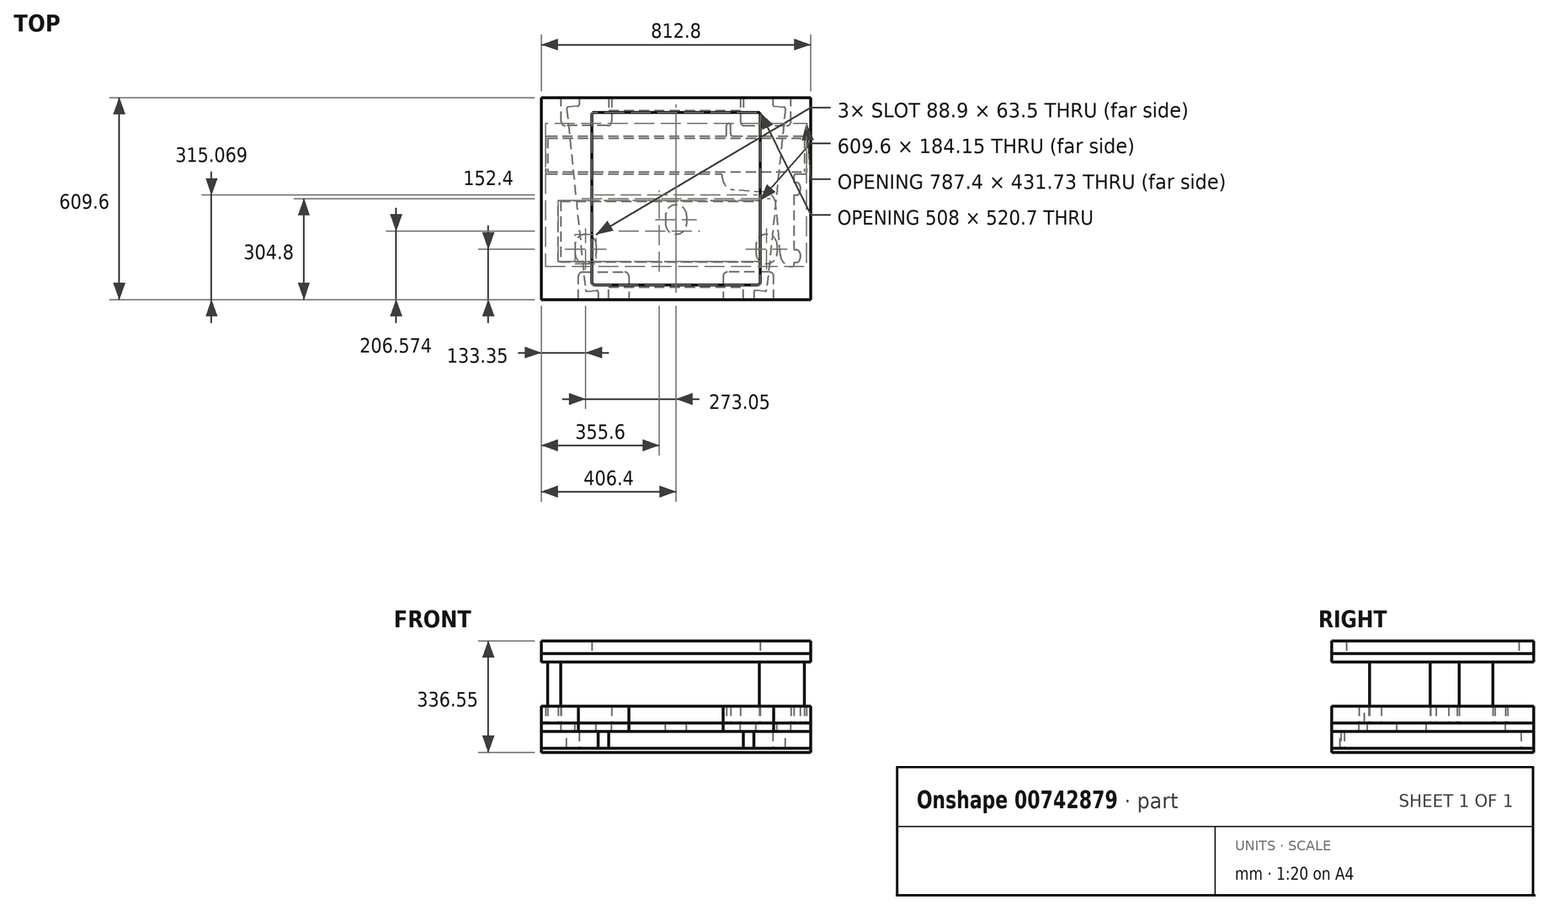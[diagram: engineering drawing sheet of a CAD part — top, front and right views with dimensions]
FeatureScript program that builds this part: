
annotation { "Feature Type Name" : "Feature", "Feature Type Description" : "" }
export const myFeature = defineFeature(function(context is Context, id is Id, definition is map)
    precondition{}
    {
        {
            var Q0;
            Q0=qCreatedBy(makeId("Top.planeOp"),FACE);
            var sketch = newSketch(context, id + "F0", { "sketchPlane" : qUnion([Q0])});
            skLineSegment(sketch, "E0.bottom", {"start": v(-406.4, 304.8) * mm, "end": v(406.4, 304.8) * mm});
            skLineSegment(sketch, "E0.top", {"start": v(-406.4, -304.8) * mm, "end": v(406.4, -304.8) * mm});
            skLineSegment(sketch, "E0.left", {"start": v(-406.4, 304.8) * mm, "end": v(-406.4, -304.8) * mm});
            skLineSegment(sketch, "E0.right", {"start": v(406.4, 304.8) * mm, "end": v(406.4, -304.8) * mm});
            skSolve(sketch);
        }
        {
            var Q0;
            Q0 = qSketchRegion(id + "F0", true);
            extrude(context, id + "F1", {"entities" : qUnion([Q0]), "depth" : 12.7 * mm, "offsetDistance" : 25.4 * mm});
        }
        {
            var Q0;
            Q0=makeQuery(id+"F1.opExtrude","CAP_FACE",FACE,{"disambiguationData":[OSD([sQuery(id+"F0.wireOp",EDGE,"E0.bottom"),sQuery(id+"F0.wireOp",EDGE,"E0.top"),sQuery(id+"F0.wireOp",EDGE,"E0.left"),sQuery(id+"F0.wireOp",EDGE,"E0.right")])],"isStart":false});
            var sketch = newSketch(context, id + "F2", { "sketchPlane" : qUnion([Q0])});
            skLineSegment(sketch, "E1", {"start": v(-292.3, 304.8) * mm, "end": v(-292.3, 279.4) * mm});
            skLineSegment(sketch, "E2", {"start": v(-292.3, 279.4) * mm, "end": v(-330.2, 275.5) * mm});
            skLineSegment(sketch, "E3", {"start": v(-330.2, 275.5) * mm, "end": v(-273.05, -280.37) * mm});
            skLineSegment(sketch, "E4", {"start": v(292.3, 304.8) * mm, "end": v(292.3, 279.4) * mm});
            skLineSegment(sketch, "E5", {"start": v(292.3, 279.4) * mm, "end": v(330.2, 275.5) * mm});
            skLineSegment(sketch, "E6", {"start": v(330.2, 275.5) * mm, "end": v(273.05, -280.37) * mm});
            skLineSegment(sketch, "E7", {"start": v(273.05, -280.37) * mm, "end": v(235.15, -276.47) * mm});
            skLineSegment(sketch, "E8", {"start": v(235.15, -276.47) * mm, "end": v(235.15, -304.8) * mm});
            skLineSegment(sketch, "E9", {"start": v(-273.05, -280.37) * mm, "end": v(-235.15, -276.47) * mm});
            skLineSegment(sketch, "E10", {"start": v(-235.15, -276.47) * mm, "end": v(-235.15, -304.8) * mm});
            skLineSegment(sketch, "E11.bottom", {"start": v(-203.2, 304.8) * mm, "end": v(203.2, 304.8) * mm});
            skLineSegment(sketch, "E11.top", {"start": v(-203.2, 266.7) * mm, "end": v(203.2, 266.7) * mm});
            skLineSegment(sketch, "E11.left", {"start": v(-203.2, 304.8) * mm, "end": v(-203.2, 266.7) * mm});
            skLineSegment(sketch, "E11.right", {"start": v(203.2, 304.8) * mm, "end": v(203.2, 266.7) * mm});
            skLineSegment(sketch, "E12.bottom", {"start": v(-203.2, -304.8) * mm, "end": v(203.2, -304.8) * mm});
            skLineSegment(sketch, "E12.top", {"start": v(-203.2, -266.7) * mm, "end": v(203.2, -266.7) * mm});
            skLineSegment(sketch, "E12.left", {"start": v(-203.2, -304.8) * mm, "end": v(-203.2, -266.7) * mm});
            skLineSegment(sketch, "E12.right", {"start": v(203.2, -304.8) * mm, "end": v(203.2, -266.7) * mm});
            skSolve(sketch);
        }
        {
            var Q0;
            Q0 = qSketchRegion(id + "F2", true);
            var Q1;
            {var subQ2=sQuery(id+"F2.wireOp",EDGE,"E1");Q1=makeQuery(id+"F2.imprint","IMPRINT",FACE,{"disambiguationData":[TD([[makeQuery(id+"F2.imprint","IMPRINT",EDGE,{"derivedFrom":subQ2}),-1.0]])]});}
            var Q2;
            {var subQ3=sQuery(id+"F2.wireOp",EDGE,"E4");Q2=makeQuery(id+"F2.imprint","IMPRINT",FACE,{"disambiguationData":[TD([[makeQuery(id+"F2.imprint","IMPRINT",EDGE,{"derivedFrom":subQ3}),1.0]])]});}
            extrude(context, id + "F3", {"entities" : qUnion([Q0, Q1, Q2]), "depth" : 50.8 * mm, "offsetDistance" : 25.4 * mm});
        }
        {
            var Q0;
            Q0=makeQuery(id+"F1.opExtrude","CAP_FACE",FACE,{"disambiguationData":[OSD([sQuery(id+"F0.wireOp",EDGE,"E0.bottom"),sQuery(id+"F0.wireOp",EDGE,"E0.top"),sQuery(id+"F0.wireOp",EDGE,"E0.left"),sQuery(id+"F0.wireOp",EDGE,"E0.right")])],"isStart":false});
            cPlane(context, id + "F4", {"entities" : qUnion([Q0]), "cplaneType" : CPlaneType.OFFSET, "offset" : 50.8 * mm, "width" : 152.4 * mm, "height" : 152.4 * mm});
        }
        {
            var Q0;
            Q0=qCreatedBy(id+"F4.planeOp",FACE);
            var sketch = newSketch(context, id + "F5", { "sketchPlane" : qUnion([Q0])});
            skLineSegment(sketch, "E13.bottom", {"start": v(-406.4, 304.8) * mm, "end": v(406.4, 304.8) * mm});
            skLineSegment(sketch, "E13.top", {"start": v(-406.4, -304.8) * mm, "end": v(406.4, -304.8) * mm});
            skLineSegment(sketch, "E13.left", {"start": v(-406.4, 304.8) * mm, "end": v(-406.4, -304.8) * mm});
            skLineSegment(sketch, "E13.right", {"start": v(406.4, 304.8) * mm, "end": v(406.4, -304.8) * mm});
            skSolve(sketch);
        }
        {
            var Q0;
            Q0 = qSketchRegion(id + "F5", true);
            extrude(context, id + "F6", {"entities" : qUnion([Q0]), "depth" : 25.4 * mm, "offsetDistance" : 25.4 * mm});
        }
        {
            var Q0;
            Q0=makeQuery(id+"F6.opExtrude","CAP_FACE",FACE,{"disambiguationData":[OSD([sQuery(id+"F5.wireOp",EDGE,"E13.bottom"),sQuery(id+"F5.wireOp",EDGE,"E13.top"),sQuery(id+"F5.wireOp",EDGE,"E13.left"),sQuery(id+"F5.wireOp",EDGE,"E13.right")])],"isStart":false});
            var sketch = newSketch(context, id + "F7", { "sketchPlane" : qUnion([Q0])});
            skLineSegment(sketch, "E14.top", {"start": v(-294.76, -304.8) * mm, "end": v(-142.36, -304.8) * mm});
            skLineSegment(sketch, "E14.right", {"start": v(-142.36, -222.05) * mm, "end": v(-142.36, -304.8) * mm});
            skLineSegment(sketch, "E15", {"start": v(0, 347.7) * mm, "end": v(0, -344.71) * mm});
            skLineSegment(sketch, "E16", {"start": v(-294.76, -304.8) * mm, "end": v(-294.76, -222.05) * mm});
            skLineSegment(sketch, "E17", {"start": v(-294.76, -222.05) * mm, "end": v(-142.36, -222.05) * mm});
            skLineSegment(sketch, "E18.right", {"start": v(-194.32, 304.8) * mm, "end": v(-194.32, 219.79) * mm});
            skLineSegment(sketch, "E19.MirrorCS", {"start": v(142.36, -222.05) * mm, "end": v(142.36, -304.8) * mm});
            skLineSegment(sketch, "E20.MirrorCS", {"start": v(294.76, -304.8) * mm, "end": v(142.36, -304.8) * mm});
            skLineSegment(sketch, "E21.MirrorCS", {"start": v(294.76, -304.8) * mm, "end": v(294.76, -222.05) * mm});
            skLineSegment(sketch, "E22.MirrorCS", {"start": v(194.32, 304.8) * mm, "end": v(194.32, 219.79) * mm});
            skLineSegment(sketch, "E23.MirrorCS", {"start": v(294.76, -222.05) * mm, "end": v(142.36, -222.05) * mm});
            skLineSegment(sketch, "E24", {"start": v(194.32, 219.79) * mm, "end": v(346.72, 219.79) * mm});
            skLineSegment(sketch, "E25", {"start": v(346.72, 219.79) * mm, "end": v(346.72, 304.8) * mm});
            skLineSegment(sketch, "E26", {"start": v(346.72, 304.8) * mm, "end": v(194.32, 304.8) * mm});
            skLineSegment(sketch, "E27", {"start": v(-194.32, 219.79) * mm, "end": v(-346.72, 219.79) * mm});
            skLineSegment(sketch, "E28", {"start": v(-346.72, 219.79) * mm, "end": v(-346.72, 304.8) * mm});
            skLineSegment(sketch, "E29", {"start": v(-346.72, 304.8) * mm, "end": v(-194.32, 304.8) * mm});
            skLineSegment(sketch, "E30.bottom", {"start": v(-273.05, -107.95) * mm, "end": v(-273.05, -107.95) * mm});
            skLineSegment(sketch, "E30.top", {"start": v(-273.05, -196.85) * mm, "end": v(-273.05, -196.85) * mm});
            skLineSegment(sketch, "E30.left", {"start": v(-304.8, -139.7) * mm, "end": v(-304.8, -165.1) * mm});
            skLineSegment(sketch, "E30.right", {"start": v(-241.3, -139.7) * mm, "end": v(-241.3, -165.1) * mm});
            skPoint(sketch, "E30.middle", {"position": v(-273.05, -152.4) * mm});
            skLineSegment(sketch, "E31.bottom", {"start": v(273.05, -107.95) * mm, "end": v(273.05, -107.95) * mm});
            skLineSegment(sketch, "E31.top", {"start": v(273.05, -196.85) * mm, "end": v(273.05, -196.85) * mm});
            skLineSegment(sketch, "E31.left", {"start": v(241.3, -139.7) * mm, "end": v(241.3, -165.1) * mm});
            skLineSegment(sketch, "E31.right", {"start": v(304.8, -139.7) * mm, "end": v(304.8, -165.1) * mm});
            skPoint(sketch, "E31.middle", {"position": v(273.05, -152.4) * mm});
            skLineSegment(sketch, "E32.bottom", {"start": v(0, -19.05) * mm, "end": v(0, -19.05) * mm});
            skLineSegment(sketch, "E32.top", {"start": v(0, -107.95) * mm, "end": v(0, -107.95) * mm});
            skLineSegment(sketch, "E32.left", {"start": v(-31.75, -50.8) * mm, "end": v(-31.75, -76.2) * mm});
            skLineSegment(sketch, "E32.right", {"start": v(31.75, -50.8) * mm, "end": v(31.75, -76.2) * mm});
            skPoint(sketch, "E32.middle", {"position": v(0, -63.5) * mm});
            skPoint(sketch, "E33.0.visualSharp", {"position": v(-304.8, -107.95) * mm});
            skArc(sketch, "E33.0.filletArc", {"start": v(-273.05, -107.95) * mm, "mid": v(-295.5, -117.25) * mm, "end": v(-304.8, -139.7) * mm});
            skPoint(sketch, "E34.0.visualSharp", {"position": v(-241.3, -107.95) * mm});
            skArc(sketch, "E34.0.filletArc", {"start": v(-241.3, -139.7) * mm, "mid": v(-250.6, -117.25) * mm, "end": v(-273.05, -107.95) * mm});
            skPoint(sketch, "E35.0.visualSharp", {"position": v(-304.8, -196.85) * mm});
            skArc(sketch, "E35.0.filletArc", {"start": v(-304.8, -165.1) * mm, "mid": v(-295.5, -187.55) * mm, "end": v(-273.05, -196.85) * mm});
            skPoint(sketch, "E36.0.visualSharp", {"position": v(-241.3, -196.85) * mm});
            skArc(sketch, "E36.0.filletArc", {"start": v(-273.05, -196.85) * mm, "mid": v(-250.6, -187.55) * mm, "end": v(-241.3, -165.1) * mm});
            skPoint(sketch, "E37.0.visualSharp", {"position": v(-31.75, -19.05) * mm});
            skArc(sketch, "E37.0.filletArc", {"start": v(0, -19.05) * mm, "mid": v(-22.45, -28.35) * mm, "end": v(-31.75, -50.8) * mm});
            skPoint(sketch, "E37.1.visualSharp", {"position": v(31.75, -19.05) * mm});
            skArc(sketch, "E37.1.filletArc", {"start": v(31.75, -50.8) * mm, "mid": v(22.45, -28.35) * mm, "end": v(0, -19.05) * mm});
            skPoint(sketch, "E38.0.visualSharp", {"position": v(-31.75, -107.95) * mm});
            skArc(sketch, "E38.0.filletArc", {"start": v(-31.75, -76.2) * mm, "mid": v(-22.45, -98.65) * mm, "end": v(0, -107.95) * mm});
            skPoint(sketch, "E39.0.visualSharp", {"position": v(31.75, -107.95) * mm});
            skArc(sketch, "E39.0.filletArc", {"start": v(0, -107.95) * mm, "mid": v(22.45, -98.65) * mm, "end": v(31.75, -76.2) * mm});
            skPoint(sketch, "E39.1.visualSharp", {"position": v(241.3, -107.95) * mm});
            skArc(sketch, "E39.1.filletArc", {"start": v(273.05, -107.95) * mm, "mid": v(250.6, -117.25) * mm, "end": v(241.3, -139.7) * mm});
            skPoint(sketch, "E39.2.visualSharp", {"position": v(304.8, -107.95) * mm});
            skArc(sketch, "E39.2.filletArc", {"start": v(304.8, -139.7) * mm, "mid": v(295.5, -117.25) * mm, "end": v(273.05, -107.95) * mm});
            skPoint(sketch, "E40.0.visualSharp", {"position": v(304.8, -196.85) * mm});
            skArc(sketch, "E40.0.filletArc", {"start": v(273.05, -196.85) * mm, "mid": v(295.5, -187.55) * mm, "end": v(304.8, -165.1) * mm});
            skPoint(sketch, "E40.1.visualSharp", {"position": v(241.3, -196.85) * mm});
            skArc(sketch, "E40.1.filletArc", {"start": v(241.3, -165.1) * mm, "mid": v(250.6, -187.55) * mm, "end": v(273.05, -196.85) * mm});
            skSolve(sketch);
        }
        {
            var Q0;
            Q0 = qSketchRegion(id + "F7", true);
            extrude(context, id + "F8", {"entities" : qUnion([Q0]), "operationType" : NewBodyOperationType.REMOVE, "oppositeDirection" : true, "depth" : 25.4 * mm, "offsetDistance" : 25.4 * mm});
        }
        {
            var Q0;
            Q0=makeQuery(id+"F6.opExtrude","CAP_FACE",FACE,{"disambiguationData":[OSD([sQuery(id+"F5.wireOp",EDGE,"E13.bottom"),sQuery(id+"F5.wireOp",EDGE,"E13.top"),sQuery(id+"F5.wireOp",EDGE,"E13.left"),sQuery(id+"F5.wireOp",EDGE,"E13.right")])],"isStart":false});
            var sketch = newSketch(context, id + "F9", { "sketchPlane" : qUnion([Q0])});
            skLineSegment(sketch, "E41", {"start": v(-406.4, -304.8) * mm, "end": v(-294.76, -304.8) * mm});
            skLineSegment(sketch, "E42", {"start": v(-294.76, -304.8) * mm, "end": v(-294.76, -222.05) * mm});
            skLineSegment(sketch, "E43", {"start": v(-294.76, -222.05) * mm, "end": v(-142.36, -222.05) * mm});
            skLineSegment(sketch, "E44", {"start": v(-142.36, -222.05) * mm, "end": v(-142.36, -304.8) * mm});
            skLineSegment(sketch, "E45", {"start": v(-142.36, -304.8) * mm, "end": v(142.36, -304.8) * mm});
            skLineSegment(sketch, "E46", {"start": v(142.36, -304.8) * mm, "end": v(142.36, -222.05) * mm});
            skLineSegment(sketch, "E47", {"start": v(142.36, -222.05) * mm, "end": v(294.76, -222.05) * mm});
            skLineSegment(sketch, "E48", {"start": v(294.76, -222.05) * mm, "end": v(294.76, -304.8) * mm});
            skLineSegment(sketch, "E49", {"start": v(294.76, -304.8) * mm, "end": v(406.4, -304.8) * mm});
            skLineSegment(sketch, "E50", {"start": v(194.32, 219.79) * mm, "end": v(194.32, 304.8) * mm});
            skLineSegment(sketch, "E51", {"start": v(194.32, 304.8) * mm, "end": v(-194.32, 304.8) * mm});
            skLineSegment(sketch, "E52", {"start": v(-194.32, 304.8) * mm, "end": v(-194.32, 219.79) * mm});
            skLineSegment(sketch, "E53.bottom", {"start": v(-393.7, 188.04) * mm, "end": v(393.7, 188.04) * mm});
            skLineSegment(sketch, "E53.top", {"start": v(-393.7, 73.74) * mm, "end": v(393.7, 73.74) * mm});
            skLineSegment(sketch, "E53.left", {"start": v(-393.7, 188.04) * mm, "end": v(-393.7, 73.74) * mm});
            skLineSegment(sketch, "E53.right", {"start": v(393.7, 188.04) * mm, "end": v(393.7, 73.74) * mm});
            skLineSegment(sketch, "E54", {"start": v(355.6, 73.74) * mm, "end": v(355.6, -205.66) * mm});
            skLineSegment(sketch, "E55", {"start": v(355.6, -205.66) * mm, "end": v(317.5, -205.66) * mm});
            skLineSegment(sketch, "E56", {"start": v(317.5, -205.66) * mm, "end": v(298.45, 16.59) * mm});
            skLineSegment(sketch, "E57", {"start": v(298.45, 16.59) * mm, "end": v(139.7, 29.29) * mm});
            skLineSegment(sketch, "E58", {"start": v(139.7, 29.29) * mm, "end": v(139.7, 73.74) * mm});
            skLineSegment(sketch, "E59.bottom", {"start": v(165.1, 188.04) * mm, "end": v(152.4, 188.04) * mm});
            skLineSegment(sketch, "E59.top", {"start": v(165.1, 226.14) * mm, "end": v(152.4, 226.14) * mm});
            skLineSegment(sketch, "E59.left", {"start": v(165.1, 188.04) * mm, "end": v(165.1, 226.14) * mm});
            skLineSegment(sketch, "E59.right", {"start": v(152.4, 188.04) * mm, "end": v(152.4, 226.14) * mm});
            skPoint(sketch, "E60.visualSharp", {"position": v(139.7, 29.29) * mm});
            skLineSegment(sketch, "E61", {"start": v(406.4, -304.8) * mm, "end": v(406.4, 304.8) * mm});
            skLineSegment(sketch, "E62", {"start": v(406.4, 304.8) * mm, "end": v(346.72, 304.8) * mm});
            skLineSegment(sketch, "E63", {"start": v(346.72, 304.8) * mm, "end": v(346.72, 219.79) * mm});
            skLineSegment(sketch, "E64", {"start": v(346.72, 219.79) * mm, "end": v(194.32, 219.79) * mm});
            skLineSegment(sketch, "E65", {"start": v(-406.4, -304.8) * mm, "end": v(-406.4, 304.8) * mm});
            skLineSegment(sketch, "E66", {"start": v(-406.4, 304.8) * mm, "end": v(-346.72, 304.8) * mm});
            skLineSegment(sketch, "E67", {"start": v(-346.72, 304.8) * mm, "end": v(-346.72, 219.79) * mm});
            skLineSegment(sketch, "E68", {"start": v(-346.72, 219.79) * mm, "end": v(-194.32, 219.79) * mm});
            skLineSegment(sketch, "E69.bottom", {"start": v(-355.6, -190.3) * mm, "end": v(254, -190.3) * mm});
            skLineSegment(sketch, "E69.top", {"start": v(-355.6, -6.15) * mm, "end": v(254, -6.15) * mm});
            skLineSegment(sketch, "E69.left", {"start": v(-355.6, -190.3) * mm, "end": v(-355.6, -6.15) * mm});
            skLineSegment(sketch, "E69.right", {"start": v(254, -190.3) * mm, "end": v(254, -6.15) * mm});
            skLineSegment(sketch, "E70.bottom", {"start": v(355.6, 48.34) * mm, "end": v(374.65, 48.34) * mm});
            skLineSegment(sketch, "E70.top", {"start": v(355.6, 10.24) * mm, "end": v(374.65, 10.24) * mm});
            skLineSegment(sketch, "E70.left", {"start": v(355.6, 48.34) * mm, "end": v(355.6, 10.24) * mm});
            skLineSegment(sketch, "E70.right", {"start": v(374.65, 48.34) * mm, "end": v(374.65, 10.24) * mm});
            skLineSegment(sketch, "E71.bottom", {"start": v(355.6, -154.86) * mm, "end": v(374.65, -154.86) * mm});
            skLineSegment(sketch, "E71.top", {"start": v(355.6, -192.96) * mm, "end": v(374.65, -192.96) * mm});
            skLineSegment(sketch, "E71.left", {"start": v(355.6, -154.86) * mm, "end": v(355.6, -192.96) * mm});
            skLineSegment(sketch, "E71.right", {"start": v(374.65, -154.86) * mm, "end": v(374.65, -192.96) * mm});
            skSolve(sketch);
        }
        {
            var Q0;
            Q0 = qSketchRegion(id + "F9", true);
            extrude(context, id + "F10", {"entities" : qUnion([Q0]), "depth" : 50.8 * mm, "offsetDistance" : 25.4 * mm});
        }
        {
            var Q0;
            Q0=qCreatedBy(id+"F4.planeOp",FACE);
            cPlane(context, id + "F11", {"entities" : qUnion([Q0]), "cplaneType" : CPlaneType.OFFSET, "offset" : 209.55 * mm, "width" : 152.4 * mm, "height" : 152.4 * mm});
        }
        {
            var Q0;
            Q0=qCreatedBy(id+"F11.planeOp",FACE);
            var sketch = newSketch(context, id + "F12", { "sketchPlane" : qUnion([Q0])});
            skLineSegment(sketch, "E72.bottom", {"start": v(-406.4, -304.8) * mm, "end": v(406.4, -304.8) * mm});
            skLineSegment(sketch, "E72.top", {"start": v(-406.4, 304.8) * mm, "end": v(406.4, 304.8) * mm});
            skLineSegment(sketch, "E72.left", {"start": v(-406.4, -304.8) * mm, "end": v(-406.4, 304.8) * mm});
            skLineSegment(sketch, "E72.right", {"start": v(406.4, -304.8) * mm, "end": v(406.4, 304.8) * mm});
            skSolve(sketch);
        }
        {
            var Q0;
            Q0 = qSketchRegion(id + "F12", true);
            extrude(context, id + "F13", {"entities" : qUnion([Q0]), "depth" : 25.4 * mm, "offsetDistance" : 25.4 * mm});
        }
        {
            var Q0;
            Q0=makeQuery(id+"F13.opExtrude","CAP_FACE",FACE,{"disambiguationData":[OSD([sQuery(id+"F12.wireOp",EDGE,"E72.bottom"),sQuery(id+"F12.wireOp",EDGE,"E72.top"),sQuery(id+"F12.wireOp",EDGE,"E72.left"),sQuery(id+"F12.wireOp",EDGE,"E72.right")])],"isStart":false});
            var sketch = newSketch(context, id + "F14", { "sketchPlane" : qUnion([Q0])});
            skLineSegment(sketch, "E73.bottom", {"start": v(-406.4, 304.8) * mm, "end": v(406.4, 304.8) * mm});
            skLineSegment(sketch, "E73.top", {"start": v(-406.4, -304.8) * mm, "end": v(406.4, -304.8) * mm});
            skLineSegment(sketch, "E73.left", {"start": v(-406.4, 304.8) * mm, "end": v(-406.4, -304.8) * mm});
            skLineSegment(sketch, "E73.right", {"start": v(406.4, 304.8) * mm, "end": v(406.4, -304.8) * mm});
            skLineSegment(sketch, "E74.bottom", {"start": v(-254, 260.35) * mm, "end": v(254, 260.35) * mm});
            skLineSegment(sketch, "E74.top", {"start": v(-254, -260.35) * mm, "end": v(254, -260.35) * mm});
            skLineSegment(sketch, "E74.left", {"start": v(-254, 260.35) * mm, "end": v(-254, -260.35) * mm});
            skLineSegment(sketch, "E74.right", {"start": v(254, 260.35) * mm, "end": v(254, -260.35) * mm});
            skSolve(sketch);
        }
        {
            var Q0;
            Q0 = qSketchRegion(id + "F14", true);
            extrude(context, id + "F15", {"entities" : qUnion([Q0]), "depth" : 38.1 * mm, "offsetDistance" : 25.4 * mm});
        }
        {
            var Q0;
            Q0=makeQuery(id+"F10.opExtrude","SWEPT_EDGE",EDGE,{"disambiguationData":[OSD([sQuery(id+"F9.wireOp",EDGE,"E57"),sQuery(id+"F9.wireOp",EDGE,"E58")])]});
            var Q1;
            Q1=makeQuery(id+"F10.opExtrude","SWEPT_EDGE",EDGE,{"disambiguationData":[OSD([sQuery(id+"F9.wireOp",EDGE,"E56"),sQuery(id+"F9.wireOp",EDGE,"E57")])]});
            var Q2;
            Q2=makeQuery(id+"F10.opExtrude","SWEPT_EDGE",EDGE,{"disambiguationData":[OSD([sQuery(id+"F9.wireOp",EDGE,"E55"),sQuery(id+"F9.wireOp",EDGE,"E56")])]});
            fillet(context, id + "F16", {"entities" : qUnion([Q0, Q1, Q2]), "radius" : 38.1 * mm, "tangentPropagation" : true, "allowEdgeOverflow" : false});
        }
        {
            var Q0;
            Q0=makeQuery(id+"F10.opExtrude","SWEPT_EDGE",EDGE,{"disambiguationData":[OSD([sQuery(id+"F9.wireOp",EDGE,"Z3YEzZHo-Bui1-ousJ-slzW-WUeqwLS6bUEM.top"),sQuery(id+"F9.wireOp",EDGE,"gvYDkn1p-4vf0-wHje-2ojT-luJldiSQSmDk.top"),sQuery(id+"F9.wireOp",EDGE,"gvYDkn1p-4vf0-wHje-2ojT-luJldiSQSmDk.right")])]});
            var Q1;
            Q1=makeQuery(id+"F10.opExtrude","SWEPT_EDGE",EDGE,{"disambiguationData":[OSD([sQuery(id+"F9.wireOp",EDGE,"Z3YEzZHo-Bui1-ousJ-slzW-WUeqwLS6bUEM.top"),sQuery(id+"F9.wireOp",EDGE,"gvYDkn1p-4vf0-wHje-2ojT-luJldiSQSmDk.top"),sQuery(id+"F9.wireOp",EDGE,"gvYDkn1p-4vf0-wHje-2ojT-luJldiSQSmDk.left")])]});
            var Q2;
            Q2=makeQuery(id+"F10.opExtrude","SWEPT_EDGE",EDGE,{"disambiguationData":[OSD([sQuery(id+"F9.wireOp",EDGE,"trNHLc45-bUhB-ut3O-UKb6-NT0g8tcLPlhB.top"),sQuery(id+"F9.wireOp",EDGE,"IcxL3pd4-v9Jh-hRel-BcxW-jEKBXCqSpwej")])]});
            var Q3;
            Q3=makeQuery(id+"F10.opExtrude","SWEPT_EDGE",EDGE,{"disambiguationData":[OSD([sQuery(id+"F9.wireOp",EDGE,"sufnx19k-zLc5-4Tfv-GUf6-5Dp0JC1L5PvA"),sQuery(id+"F9.wireOp",EDGE,"gvYDkn1p-4vf0-wHje-2ojT-luJldiSQSmDk.bottom"),sQuery(id+"F9.wireOp",EDGE,"gvYDkn1p-4vf0-wHje-2ojT-luJldiSQSmDk.right")])]});
            var Q4;
            Q4=makeQuery(id+"F10.opExtrude","SWEPT_EDGE",EDGE,{"disambiguationData":[OSD([sQuery(id+"F9.wireOp",EDGE,"G701UPqg-fKqI-65K2-tPSG-xiTPsywNCcCX"),sQuery(id+"F9.wireOp",EDGE,"sufnx19k-zLc5-4Tfv-GUf6-5Dp0JC1L5PvA")])]});
            var Q5;
            Q5=makeQuery(id+"F10.opExtrude","SWEPT_EDGE",EDGE,{"disambiguationData":[OSD([sQuery(id+"F9.wireOp",EDGE,"trNHLc45-bUhB-ut3O-UKb6-NT0g8tcLPlhB.top"),sQuery(id+"F9.wireOp",EDGE,"trNHLc45-bUhB-ut3O-UKb6-NT0g8tcLPlhB.left")])]});
            var Q6;
            Q6=makeQuery(id+"F10.opExtrude","SWEPT_EDGE",EDGE,{"disambiguationData":[OSD([sQuery(id+"F9.wireOp",EDGE,"E53.top"),sQuery(id+"F9.wireOp",EDGE,"E58")])]});
            var Q7;
            Q7=makeQuery(id+"F10.opExtrude","SWEPT_EDGE",EDGE,{"disambiguationData":[OSD([sQuery(id+"F9.wireOp",EDGE,"E53.bottom"),sQuery(id+"F9.wireOp",EDGE,"E59.bottom"),sQuery(id+"F9.wireOp",EDGE,"E59.right")])]});
            var Q8;
            Q8=makeQuery(id+"F10.opExtrude","SWEPT_EDGE",EDGE,{"disambiguationData":[OSD([sQuery(id+"F9.wireOp",EDGE,"E53.bottom"),sQuery(id+"F9.wireOp",EDGE,"E59.bottom"),sQuery(id+"F9.wireOp",EDGE,"E59.left")])]});
            var Q9;
            Q9=makeQuery(id+"F10.opExtrude","SWEPT_EDGE",EDGE,{"disambiguationData":[OSD([sQuery(id+"F9.wireOp",EDGE,"E53.bottom"),sQuery(id+"F9.wireOp",EDGE,"E53.right")])]});
            var Q10;
            Q10=makeQuery(id+"F10.opExtrude","SWEPT_EDGE",EDGE,{"disambiguationData":[OSD([sQuery(id+"F9.wireOp",EDGE,"E53.top"),sQuery(id+"F9.wireOp",EDGE,"E53.right")])]});
            var Q11;
            Q11=makeQuery(id+"F10.opExtrude","SWEPT_EDGE",EDGE,{"disambiguationData":[OSD([sQuery(id+"F9.wireOp",EDGE,"E53.top"),sQuery(id+"F9.wireOp",EDGE,"E54")])]});
            var Q12;
            Q12=makeQuery(id+"F10.opExtrude","SWEPT_EDGE",EDGE,{"disambiguationData":[OSD([sQuery(id+"F9.wireOp",EDGE,"E54"),sQuery(id+"F9.wireOp",EDGE,"E55")])]});
            var Q13;
            Q13=makeQuery(id+"F10.opExtrude","SWEPT_EDGE",EDGE,{"disambiguationData":[OSD([sQuery(id+"F9.wireOp",EDGE,"E53.bottom"),sQuery(id+"F9.wireOp",EDGE,"E53.left")])]});
            var Q14;
            Q14=makeQuery(id+"F10.opExtrude","SWEPT_EDGE",EDGE,{"disambiguationData":[OSD([sQuery(id+"F9.wireOp",EDGE,"E53.top"),sQuery(id+"F9.wireOp",EDGE,"E53.left")])]});
            var Q15;
            Q15=makeQuery(id+"F10.opExtrude","SWEPT_EDGE",EDGE,{"disambiguationData":[OSD([sQuery(id+"F9.wireOp",EDGE,"zyW1Xxlw-5Evh-1siC-1rJg-L85HlnxgWExc.bottom"),sQuery(id+"F9.wireOp",EDGE,"zyW1Xxlw-5Evh-1siC-1rJg-L85HlnxgWExc.left")])]});
            var Q16;
            Q16=makeQuery(id+"F10.opExtrude","SWEPT_EDGE",EDGE,{"disambiguationData":[OSD([sQuery(id+"F9.wireOp",EDGE,"MilimUlD-Aw0j-xEc8-R3LJ-kISBP3y56L3H.bottom"),sQuery(id+"F9.wireOp",EDGE,"MilimUlD-Aw0j-xEc8-R3LJ-kISBP3y56L3H.left")])]});
            var Q17;
            Q17=makeQuery(id+"F10.opExtrude","SWEPT_EDGE",EDGE,{"disambiguationData":[OSD([sQuery(id+"F9.wireOp",EDGE,"zyW1Xxlw-5Evh-1siC-1rJg-L85HlnxgWExc.bottom"),sQuery(id+"F9.wireOp",EDGE,"zyW1Xxlw-5Evh-1siC-1rJg-L85HlnxgWExc.right")])]});
            var Q18;
            Q18=makeQuery(id+"F10.opExtrude","SWEPT_EDGE",EDGE,{"disambiguationData":[OSD([sQuery(id+"F9.wireOp",EDGE,"MilimUlD-Aw0j-xEc8-R3LJ-kISBP3y56L3H.bottom"),sQuery(id+"F9.wireOp",EDGE,"MilimUlD-Aw0j-xEc8-R3LJ-kISBP3y56L3H.right")])]});
            var Q19;
            Q19=makeQuery(id+"F10.opExtrude","SWEPT_EDGE",EDGE,{"disambiguationData":[OSD([sQuery(id+"F9.wireOp",EDGE,"MilimUlD-Aw0j-xEc8-R3LJ-kISBP3y56L3H.top"),sQuery(id+"F9.wireOp",EDGE,"MilimUlD-Aw0j-xEc8-R3LJ-kISBP3y56L3H.right")])]});
            var Q20;
            Q20=makeQuery(id+"F10.opExtrude","SWEPT_EDGE",EDGE,{"disambiguationData":[OSD([sQuery(id+"F9.wireOp",EDGE,"zyW1Xxlw-5Evh-1siC-1rJg-L85HlnxgWExc.top"),sQuery(id+"F9.wireOp",EDGE,"zyW1Xxlw-5Evh-1siC-1rJg-L85HlnxgWExc.right")])]});
            var Q21;
            Q21=makeQuery(id+"F10.opExtrude","SWEPT_EDGE",EDGE,{"disambiguationData":[OSD([sQuery(id+"F9.wireOp",EDGE,"MilimUlD-Aw0j-xEc8-R3LJ-kISBP3y56L3H.top"),sQuery(id+"F9.wireOp",EDGE,"MilimUlD-Aw0j-xEc8-R3LJ-kISBP3y56L3H.left")])]});
            var Q22;
            Q22=makeQuery(id+"F10.opExtrude","SWEPT_EDGE",EDGE,{"disambiguationData":[OSD([sQuery(id+"F9.wireOp",EDGE,"zyW1Xxlw-5Evh-1siC-1rJg-L85HlnxgWExc.top"),sQuery(id+"F9.wireOp",EDGE,"zyW1Xxlw-5Evh-1siC-1rJg-L85HlnxgWExc.left")])]});
            var Q23;
            Q23=makeQuery(id+"F10.opExtrude","SWEPT_EDGE",EDGE,{"disambiguationData":[OSD([sQuery(id+"F9.wireOp",EDGE,"E59.top"),sQuery(id+"F9.wireOp",EDGE,"E59.left")])]});
            var Q24;
            Q24=makeQuery(id+"F10.opExtrude","SWEPT_EDGE",EDGE,{"disambiguationData":[OSD([sQuery(id+"F9.wireOp",EDGE,"E59.top"),sQuery(id+"F9.wireOp",EDGE,"E59.right")])]});
            var Q25;
            Q25=makeQuery(id+"F10.opExtrude","SWEPT_EDGE",EDGE,{"disambiguationData":[OSD([sQuery(id+"F9.wireOp",EDGE,"Z3YEzZHo-Bui1-ousJ-slzW-WUeqwLS6bUEM.left"),sQuery(id+"F9.wireOp",EDGE,"hOsIz9KZ-M8hK-xMSw-Pl1F-AwsMzmgApuak")])]});
            var Q26;
            Q26=makeQuery(id+"F10.opExtrude","SWEPT_EDGE",EDGE,{"disambiguationData":[OSD([sQuery(id+"F9.wireOp",EDGE,"Z3YEzZHo-Bui1-ousJ-slzW-WUeqwLS6bUEM.right"),sQuery(id+"F9.wireOp",EDGE,"hOsIz9KZ-M8hK-xMSw-Pl1F-AwsMzmgApuak")])]});
            var Q27;
            Q27=makeQuery(id+"F10.opExtrude","SWEPT_EDGE",EDGE,{"disambiguationData":[OSD([sQuery(id+"F9.wireOp",EDGE,"Z3YEzZHo-Bui1-ousJ-slzW-WUeqwLS6bUEM.top"),sQuery(id+"F9.wireOp",EDGE,"Z3YEzZHo-Bui1-ousJ-slzW-WUeqwLS6bUEM.right")])]});
            var Q28;
            Q28=makeQuery(id+"F10.opExtrude","SWEPT_EDGE",EDGE,{"disambiguationData":[OSD([sQuery(id+"F9.wireOp",EDGE,"Z3YEzZHo-Bui1-ousJ-slzW-WUeqwLS6bUEM.top"),sQuery(id+"F9.wireOp",EDGE,"Z3YEzZHo-Bui1-ousJ-slzW-WUeqwLS6bUEM.left")])]});
            fillet(context, id + "F17", {"entities" : qUnion([Q0, Q1, Q2, Q3, Q4, Q5, Q6, Q7, Q8, Q9, Q10, Q11, Q12, Q13, Q14, Q15, Q16, Q17, Q18, Q19, Q20, Q21, Q22, Q23, Q24, Q25, Q26, Q27, Q28]), "radius" : 5.08 * mm, "tangentPropagation" : true, "allowEdgeOverflow" : false});
        }
        {
            var Q0;
            Q0=makeQuery(id+"F6.opExtrude","CAP_FACE",FACE,{"disambiguationData":[OSD([sQuery(id+"F5.wireOp",EDGE,"E13.bottom"),sQuery(id+"F5.wireOp",EDGE,"E13.top"),sQuery(id+"F5.wireOp",EDGE,"E13.left"),sQuery(id+"F5.wireOp",EDGE,"E13.right")])],"isStart":false});
            var sketch = newSketch(context, id + "F18", { "sketchPlane" : qUnion([Q0])});
            skLineSegment(sketch, "E75.bottom", {"start": v(-387.35, 181.69) * mm, "end": v(387.35, 181.69) * mm});
            skLineSegment(sketch, "E75.top", {"start": v(-387.35, 80.09) * mm, "end": v(387.35, 80.09) * mm});
            skLineSegment(sketch, "E75.left", {"start": v(-387.35, 181.69) * mm, "end": v(-387.35, 80.09) * mm});
            skLineSegment(sketch, "E75.right", {"start": v(387.35, 181.69) * mm, "end": v(387.35, 80.09) * mm});
            skLineSegment(sketch, "E76.bottom", {"start": v(-348.41, -7.87) * mm, "end": v(250.82, -7.87) * mm});
            skLineSegment(sketch, "E76.top", {"start": v(-348.41, -191.08) * mm, "end": v(250.83, -191.08) * mm});
            skLineSegment(sketch, "E76.left", {"start": v(-348.41, -7.87) * mm, "end": v(-348.41, -191.08) * mm});
            skLineSegment(sketch, "E76.right", {"start": v(250.82, -7.87) * mm, "end": v(250.83, -191.08) * mm});
            skSolve(sketch);
        }
        {
            var Q0;
            Q0 = qSketchRegion(id + "F18", true);
            extrude(context, id + "F19", {"entities" : qUnion([Q0]), "depth" : 184.15 * mm, "offsetDistance" : 25.4 * mm});
        }
        {
            var Q0;
            Q0=makeQuery(id+"F15.opExtrude","SWEPT_EDGE",EDGE,{"disambiguationData":[OSD([sQuery(id+"F14.wireOp",EDGE,"E74.bottom"),sQuery(id+"F14.wireOp",EDGE,"E74.left")])]});
            var Q1;
            Q1=makeQuery(id+"F15.opExtrude","SWEPT_EDGE",EDGE,{"disambiguationData":[OSD([sQuery(id+"F14.wireOp",EDGE,"E74.bottom"),sQuery(id+"F14.wireOp",EDGE,"E74.right")])]});
            var Q2;
            Q2=makeQuery(id+"F15.opExtrude","SWEPT_EDGE",EDGE,{"disambiguationData":[OSD([sQuery(id+"F14.wireOp",EDGE,"E74.top"),sQuery(id+"F14.wireOp",EDGE,"E74.left")])]});
            var Q3;
            Q3=makeQuery(id+"F15.opExtrude","SWEPT_EDGE",EDGE,{"disambiguationData":[OSD([sQuery(id+"F14.wireOp",EDGE,"E74.top"),sQuery(id+"F14.wireOp",EDGE,"E74.right")])]});
            fillet(context, id + "F20", {"entities" : qUnion([Q0, Q1, Q2, Q3]), "radius" : 6.35 * mm, "tangentPropagation" : true, "allowEdgeOverflow" : false});
        }
        {
            var Q0;
            Q0=makeQuery(id+"F10.opExtrude","SWEPT_EDGE",EDGE,{"disambiguationData":[OSD([sQuery(id+"F9.wireOp",EDGE,"E42"),sQuery(id+"F9.wireOp",EDGE,"E43")])]});
            var Q1;
            Q1=makeQuery(id+"F8.boolean.opBoolean","COPY",EDGE,{"derivedFrom":makeQuery(id+"F8.opExtrude","SWEPT_EDGE",EDGE,{"disambiguationData":[OSD([sQuery(id+"F7.wireOp",EDGE,"E16"),sQuery(id+"F7.wireOp",EDGE,"E17")])]})});
            var Q2;
            Q2=makeQuery(id+"F8.boolean.opBoolean","COPY",EDGE,{"derivedFrom":makeQuery(id+"F8.opExtrude","SWEPT_EDGE",EDGE,{"disambiguationData":[OSD([sQuery(id+"F7.wireOp",EDGE,"E14.right"),sQuery(id+"F7.wireOp",EDGE,"E17")])]})});
            var Q3;
            Q3=makeQuery(id+"F10.opExtrude","SWEPT_EDGE",EDGE,{"disambiguationData":[OSD([sQuery(id+"F9.wireOp",EDGE,"E43"),sQuery(id+"F9.wireOp",EDGE,"E44")])]});
            var Q4;
            Q4=makeQuery(id+"F10.opExtrude","SWEPT_EDGE",EDGE,{"disambiguationData":[OSD([sQuery(id+"F9.wireOp",EDGE,"E47"),sQuery(id+"F9.wireOp",EDGE,"E48")])]});
            var Q5;
            Q5=makeQuery(id+"F8.boolean.opBoolean","COPY",EDGE,{"derivedFrom":makeQuery(id+"F8.opExtrude","SWEPT_EDGE",EDGE,{"disambiguationData":[OSD([sQuery(id+"F7.wireOp",EDGE,"E21.MirrorCS"),sQuery(id+"F7.wireOp",EDGE,"E23.MirrorCS")])]})});
            var Q6;
            Q6=makeQuery(id+"F8.boolean.opBoolean","COPY",EDGE,{"derivedFrom":makeQuery(id+"F8.opExtrude","SWEPT_EDGE",EDGE,{"disambiguationData":[OSD([sQuery(id+"F7.wireOp",EDGE,"E19.MirrorCS"),sQuery(id+"F7.wireOp",EDGE,"E23.MirrorCS")])]})});
            var Q7;
            Q7=makeQuery(id+"F10.opExtrude","SWEPT_EDGE",EDGE,{"disambiguationData":[OSD([sQuery(id+"F9.wireOp",EDGE,"E46"),sQuery(id+"F9.wireOp",EDGE,"E47")])]});
            var Q8;
            Q8=makeQuery(id+"F8.boolean.opBoolean","COPY",EDGE,{"derivedFrom":makeQuery(id+"F8.opExtrude","SWEPT_EDGE",EDGE,{"disambiguationData":[OSD([sQuery(id+"F7.wireOp",EDGE,"E22.MirrorCS"),sQuery(id+"F7.wireOp",EDGE,"22feb73b-cf35-4518-a9a2-765e4625934d7.MirrorCS")])]})});
            var Q9;
            Q9=makeQuery(id+"F8.boolean.opBoolean","COPY",EDGE,{"derivedFrom":makeQuery(id+"F8.opExtrude","SWEPT_EDGE",EDGE,{"disambiguationData":[OSD([sQuery(id+"F7.wireOp",EDGE,"E18.top"),sQuery(id+"F7.wireOp",EDGE,"E18.right")])]})});
            var Q10;
            Q10=makeQuery(id+"F10.opExtrude","SWEPT_EDGE",EDGE,{"disambiguationData":[OSD([sQuery(id+"F9.wireOp",EDGE,"E52"),sQuery(id+"F9.wireOp",EDGE,"E68")])]});
            var Q11;
            Q11=makeQuery(id+"F10.opExtrude","SWEPT_EDGE",EDGE,{"disambiguationData":[OSD([sQuery(id+"F9.wireOp",EDGE,"E50"),sQuery(id+"F9.wireOp",EDGE,"E64")])]});
            var Q12;
            Q12=makeQuery(id+"F10.opExtrude","SWEPT_EDGE",EDGE,{"disambiguationData":[OSD([sQuery(id+"F9.wireOp",EDGE,"E63"),sQuery(id+"F9.wireOp",EDGE,"E64")])]});
            var Q13;
            Q13=makeQuery(id+"F8.boolean.opBoolean","COPY",EDGE,{"derivedFrom":makeQuery(id+"F8.opExtrude","SWEPT_EDGE",EDGE,{"disambiguationData":[OSD([sQuery(id+"F7.wireOp",EDGE,"E24"),sQuery(id+"F7.wireOp",EDGE,"E25")])]})});
            var Q14;
            Q14=makeQuery(id+"F8.boolean.opBoolean","COPY",EDGE,{"derivedFrom":makeQuery(id+"F8.opExtrude","SWEPT_EDGE",EDGE,{"disambiguationData":[OSD([sQuery(id+"F7.wireOp",EDGE,"E27"),sQuery(id+"F7.wireOp",EDGE,"E28")])]})});
            var Q15;
            Q15=makeQuery(id+"F10.opExtrude","SWEPT_EDGE",EDGE,{"disambiguationData":[OSD([sQuery(id+"F9.wireOp",EDGE,"E67"),sQuery(id+"F9.wireOp",EDGE,"E68")])]});
            var Q16;
            Q16=makeQuery(id+"F10.opExtrude","SWEPT_EDGE",EDGE,{"disambiguationData":[OSD([sQuery(id+"F9.wireOp",EDGE,"E70.bottom"),sQuery(id+"F9.wireOp",EDGE,"E70.right")])]});
            var Q17;
            Q17=makeQuery(id+"F10.opExtrude","SWEPT_EDGE",EDGE,{"disambiguationData":[OSD([sQuery(id+"F9.wireOp",EDGE,"E71.bottom"),sQuery(id+"F9.wireOp",EDGE,"E71.right")])]});
            var Q18;
            Q18=makeQuery(id+"F10.opExtrude","SWEPT_EDGE",EDGE,{"disambiguationData":[OSD([sQuery(id+"F9.wireOp",EDGE,"E70.top"),sQuery(id+"F9.wireOp",EDGE,"E70.right")])]});
            var Q19;
            Q19=makeQuery(id+"F10.opExtrude","SWEPT_EDGE",EDGE,{"disambiguationData":[OSD([sQuery(id+"F9.wireOp",EDGE,"E71.top"),sQuery(id+"F9.wireOp",EDGE,"E71.right")])]});
            fillet(context, id + "F21", {"entities" : qUnion([Q0, Q1, Q2, Q3, Q4, Q5, Q6, Q7, Q8, Q9, Q10, Q11, Q12, Q13, Q14, Q15, Q16, Q17, Q18, Q19]), "radius" : 12.7 * mm, "tangentPropagation" : true, "allowEdgeOverflow" : false});
        }
        {
            var Q0;
            Q0=makeQuery(id+"F3.opExtrude","SWEPT_EDGE",EDGE,{"disambiguationData":[OSD([sQuery(id+"F2.wireOp",EDGE,"E2"),sQuery(id+"F2.wireOp",EDGE,"E3")])]});
            var Q1;
            Q1=makeQuery(id+"F3.opExtrude","SWEPT_EDGE",EDGE,{"disambiguationData":[OSD([sQuery(id+"F2.wireOp",EDGE,"E1"),sQuery(id+"F2.wireOp",EDGE,"E2")])]});
            var Q2;
            Q2=makeQuery(id+"F3.opExtrude","SWEPT_EDGE",EDGE,{"disambiguationData":[OSD([sQuery(id+"F2.wireOp",EDGE,"E5"),sQuery(id+"F2.wireOp",EDGE,"E6")])]});
            var Q3;
            Q3=makeQuery(id+"F3.opExtrude","SWEPT_EDGE",EDGE,{"disambiguationData":[OSD([sQuery(id+"F2.wireOp",EDGE,"E4"),sQuery(id+"F2.wireOp",EDGE,"E5")])]});
            var Q4;
            Q4=makeQuery(id+"F3.opExtrude","SWEPT_EDGE",EDGE,{"disambiguationData":[OSD([sQuery(id+"F2.wireOp",EDGE,"E6"),sQuery(id+"F2.wireOp",EDGE,"E7")])]});
            var Q5;
            Q5=makeQuery(id+"F3.opExtrude","SWEPT_EDGE",EDGE,{"disambiguationData":[OSD([sQuery(id+"F2.wireOp",EDGE,"E3"),sQuery(id+"F2.wireOp",EDGE,"E9")])]});
            var Q6;
            Q6=makeQuery(id+"F3.opExtrude","SWEPT_EDGE",EDGE,{"disambiguationData":[OSD([sQuery(id+"F2.wireOp",EDGE,"E9"),sQuery(id+"F2.wireOp",EDGE,"E10")])]});
            var Q7;
            Q7=makeQuery(id+"F3.opExtrude","SWEPT_EDGE",EDGE,{"disambiguationData":[OSD([sQuery(id+"F2.wireOp",EDGE,"E7"),sQuery(id+"F2.wireOp",EDGE,"E8")])]});
            fillet(context, id + "F22", {"entities" : qUnion([Q0, Q1, Q2, Q3, Q4, Q5, Q6, Q7]), "radius" : 5.08 * mm, "tangentPropagation" : true, "allowEdgeOverflow" : false});
        }
    });
